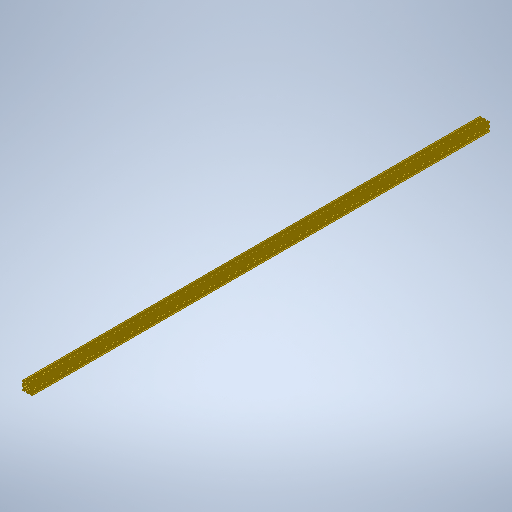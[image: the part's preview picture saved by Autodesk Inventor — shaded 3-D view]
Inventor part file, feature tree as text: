
AUTODESK INVENTOR PART (.ipt)
format: ipt  version: 2025.2 (Build 292293000, 293)  size: 481,792 bytes
history: native  units: mm
features: mirror x2, other x1, extrude x1, fillet x1, sketch x1
ambient origin geometry x8: Origin, YZ Plane, XZ Plane, XY Plane, X Axis, Y Axis, Z Axis, Center Point
bodies: Body1 (feature_tree)
feature tree (6):
  other  "Sólido1"
  extrude  "Extrusão1"  Depth=20.0mm
  mirror  "Espelhar1"
  mirror  "Espelhar2"
  fillet  "Arredondamento1"  Radius=6.2mm
  sketch  "Esboço1"  dims[d1=40.0mm d2=20.0mm d3=6.2mm d4=20.0mm d5=6.0mm d7=2.0mm d9=5.0mm d10=10.0mm d14=6.0mm d15=0.5mm d16=0.5mm d19=4.0mm d20=0.694219mm d21=1.0mm d24=0.695838mm d25=2000.0mm d26=0.0mm d27=1.0mm]
